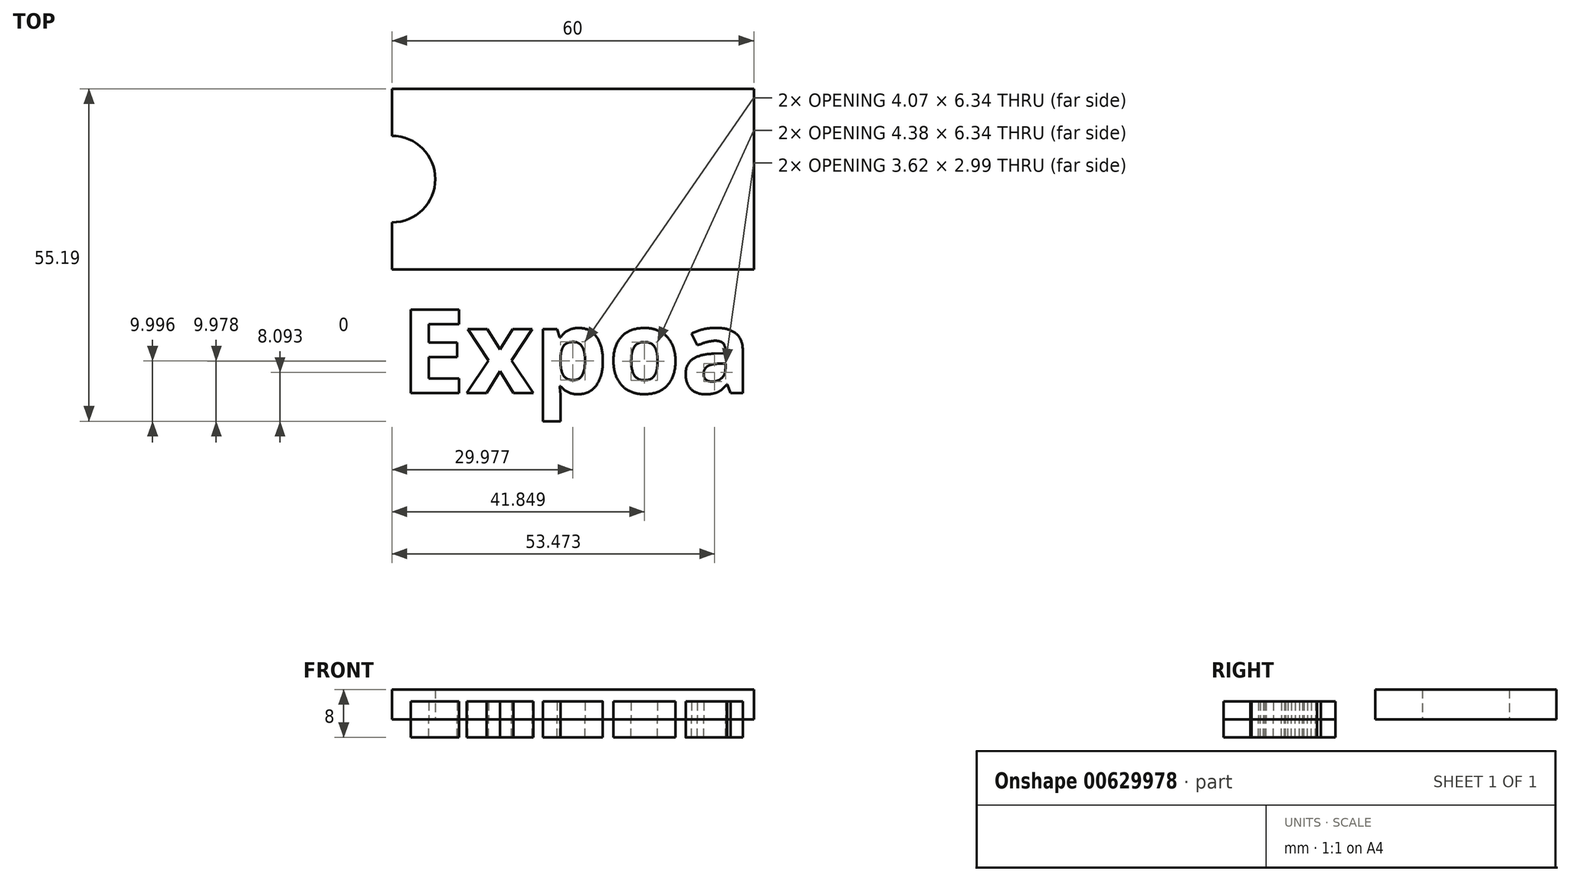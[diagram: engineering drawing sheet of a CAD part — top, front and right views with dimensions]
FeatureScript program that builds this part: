
annotation { "Feature Type Name" : "Feature", "Feature Type Description" : "" }
export const myFeature = defineFeature(function(context is Context, id is Id, definition is map)
    precondition{}
    {
        {
            var Q0;
            Q0=qCreatedBy(makeId("Top.planeOp"),FACE);
            var sketch = newSketch(context, id + "F0", { "sketchPlane" : qUnion([Q0])});
            skLineSegment(sketch, "E0.bottom", {"start": v(30, -15) * mm, "end": v(-30, -15) * mm});
            skLineSegment(sketch, "E0.top", {"start": v(30, 15) * mm, "end": v(-30, 15) * mm});
            skLineSegment(sketch, "E0.left", {"start": v(30, -15) * mm, "end": v(30, 15) * mm});
            skLineSegment(sketch, "E0.right", {"start": v(-30, -15) * mm, "end": v(-30, 15) * mm});
            skPoint(sketch, "E0.middle", {"position": v(0, 0) * mm});
            skCircle(sketch, "E1", {"center": v(-30, 0) * mm, "radius": 7.18 * mm});
            skSolve(sketch);
        }
        {
            var Q0;
            Q0=makeQuery(id+"F0.imprint","IMPRINT",FACE,{"disambiguationData":[TD([[makeQuery(id+"F0.imprint","IMPRINT",EDGE,{"derivedFrom":sQuery(id+"F0.wireOp",EDGE,"E0.bottom")}),-1.0]])]});
            extrude(context, id + "F1", {"entities" : qUnion([Q0]), "depth" : 5 * mm, "offsetDistance" : 25 * mm});
        }
        {
            var Q0;
            Q0=makeQuery(id+"F1.opExtrude","SWEPT_EDGE",EDGE,{"disambiguationData":[OSD([sQuery(id+"F0.wireOp",EDGE,"E0.bottom"),sQuery(id+"F0.wireOp",EDGE,"E0.right")])]});
            var Q1;
            Q1=makeQuery(id+"F1.opExtrude","SWEPT_EDGE",EDGE,{"disambiguationData":[OSD([sQuery(id+"F0.wireOp",EDGE,"E0.bottom"),sQuery(id+"F0.wireOp",EDGE,"E0.left")])]});
            var Q2;
            Q2=makeQuery(id+"F1.opExtrude","SWEPT_EDGE",EDGE,{"disambiguationData":[OSD([sQuery(id+"F0.wireOp",EDGE,"E0.top"),sQuery(id+"F0.wireOp",EDGE,"E0.left")])]});
            var Q3;
            Q3=makeQuery(id+"F1.opExtrude","SWEPT_EDGE",EDGE,{"disambiguationData":[OSD([sQuery(id+"F0.wireOp",EDGE,"E0.top"),sQuery(id+"F0.wireOp",EDGE,"E0.right")])]});
            fillet(context, id + "F2", {"entities" : qUnion([Q0, Q1, Q2, Q3]), "radius" : 5 * mm, "tangentPropagation" : true, "allowEdgeOverflow" : false});
        }
        {
            var Q0;
            {var subQ0=sQuery(id+"F0.wireOp",EDGE,"E1");var subQ1=sQuery(id+"F0.wireOp",EDGE,"E0.right");var subQ2=makeQuery(id+"F0.imprint","INTERSECT",VERTEX,{"disambiguationData":[OD(0.0)],"derivedFrom":[subQ1,subQ0]});Q0=makeQuery(id+"F0.imprint","IMPRINT",FACE,{"disambiguationData":[TD([[makeQuery(id+"F0.imprint","IMPRINT",EDGE,{"disambiguationData":[TD([[subQ2,-1.0]])],"derivedFrom":subQ1}),-1.0]])]});}
            var Q1;
            {var subQ0=sQuery(id+"F0.wireOp",EDGE,"E1");var subQ1=sQuery(id+"F0.wireOp",EDGE,"E0.right");var subQ2=makeQuery(id+"F0.imprint","INTERSECT",VERTEX,{"disambiguationData":[OD(0.0)],"derivedFrom":[subQ1,subQ0]});Q1=makeQuery(id+"F0.imprint","IMPRINT",FACE,{"disambiguationData":[TD([[makeQuery(id+"F0.imprint","IMPRINT",EDGE,{"disambiguationData":[TD([[subQ2,-1.0]])],"derivedFrom":subQ1}),1.0]])]});}
            extrude(context, id + "F3", {"entities" : qUnion([Q0, Q1]), "operationType" : NewBodyOperationType.ADD, "depth" : 5 * mm, "offsetDistance" : 25 * mm});
        }
        {
            var Q0;
            {var subQ0=sQuery(id+"F0.wireOp",EDGE,"E1");Q0=makeQuery(id+"F3.boolean.opBoolean","MERGE",FACE,{"derivedFrom":[makeQuery(id+"F1.opExtrude","CAP_FACE",FACE,{"disambiguationData":[OSD([sQuery(id+"F0.wireOp",EDGE,"E0.bottom"),sQuery(id+"F0.wireOp",EDGE,"E0.top"),sQuery(id+"F0.wireOp",EDGE,"E0.left"),sQuery(id+"F0.wireOp",EDGE,"E0.right"),subQ0])],"isStart":false}),makeQuery(id+"F3.opExtrude","CAP_FACE",FACE,{"disambiguationData":[OSD([subQ0])],"isStart":false})]});}
            var sketch = newSketch(context, id + "F4", { "sketchPlane" : qUnion([Q0])});
            skCircle(sketch, "E2", {"center": v(-31.84, 0) * mm, "radius": 1.79 * mm});
            skCircle(sketch, "E3", {"center": v(-31.84, 0) * mm, "radius": 3.5 * mm});
            skSolve(sketch);
        }
        {
            var Q0;
            Q0=makeQuery(id+"F4.imprint","IMPRINT",FACE,{"disambiguationData":[TD([[makeQuery(id+"F4.imprint","IMPRINT",EDGE,{"derivedFrom":sQuery(id+"F4.wireOp",EDGE,"E2")}),1.0]])]});
            extrude(context, id + "F5", {"entities" : qUnion([Q0]), "operationType" : NewBodyOperationType.REMOVE, "oppositeDirection" : true, "depth" : 25 * mm, "offsetDistance" : 25 * mm});
        }
        {
            var Q0;
            Q0=qCreatedBy(makeId("Top.planeOp"),FACE);
            var sketch = newSketch(context, id + "F6", { "sketchPlane" : qUnion([Q0])});
            skText(sketch, "E4", { "text": "Expoa", "fontName": "OpenSans-Bold.ttf"});
            const initialGuessF6  = {"E4": [-0.0286, -0.03552, 1, 0, 0.014]};
            skSetInitialGuess(sketch, initialGuessF6);
            skSolve(sketch);
        }
        {
            var Q0;
            Q0=makeQuery(id+"F6.imprint","IMPRINT",FACE,{"disambiguationData":[TD([[makeQuery(id+"F6.imprint","IMPRINT",EDGE,{"derivedFrom":sQuery(id+"F6.wireOp",EDGE,"E4.sketch_text.stroke-0")}),-1.0]])]});
            var Q1;
            Q1=makeQuery(id+"F6.imprint","IMPRINT",FACE,{"disambiguationData":[TD([[makeQuery(id+"F6.imprint","IMPRINT",EDGE,{"derivedFrom":sQuery(id+"F6.wireOp",EDGE,"E4.sketch_text.stroke-12")}),-1.0]])]});
            var Q2;
            Q2=makeQuery(id+"F6.imprint","IMPRINT",FACE,{"disambiguationData":[TD([[makeQuery(id+"F6.imprint","IMPRINT",EDGE,{"derivedFrom":sQuery(id+"F6.wireOp",EDGE,"E4.sketch_text.stroke-24")}),-1.0]])]});
            var Q3;
            Q3=makeQuery(id+"F6.imprint","IMPRINT",FACE,{"disambiguationData":[TD([[makeQuery(id+"F6.imprint","IMPRINT",EDGE,{"derivedFrom":sQuery(id+"F6.wireOp",EDGE,"E4.sketch_text.stroke-47")}),-1.0]])]});
            var Q4;
            Q4=makeQuery(id+"F6.imprint","IMPRINT",FACE,{"disambiguationData":[TD([[makeQuery(id+"F6.imprint","IMPRINT",EDGE,{"derivedFrom":sQuery(id+"F6.wireOp",EDGE,"E4.sketch_text.stroke-65")}),-1.0]])]});
            extrude(context, id + "F7", {"entities" : qUnion([Q0, Q1, Q2, Q3, Q4]), "operationType" : NewBodyOperationType.ADD, "oppositeDirection" : true, "depth" : 3 * mm, "offsetDistance" : 25 * mm});
        }
        {
            var Q0;
            Q0=makeQuery(id+"F4.imprint","IMPRINT",FACE,{"disambiguationData":[TD([[makeQuery(id+"F4.imprint","IMPRINT",EDGE,{"derivedFrom":sQuery(id+"F4.wireOp",EDGE,"E2")}),-1.0]])]});
            var Q1;
            Q1=makeQuery(id+"F4.imprint","IMPRINT",FACE,{"disambiguationData":[TD([[makeQuery(id+"F4.imprint","IMPRINT",EDGE,{"derivedFrom":sQuery(id+"F4.wireOp",EDGE,"E2")}),1.0]])]});
            extrude(context, id + "F8", {"entities" : qUnion([Q0, Q1]), "operationType" : NewBodyOperationType.REMOVE, "oppositeDirection" : true, "depth" : 25 * mm, "offsetDistance" : 25 * mm});
        }
        {
            var Q0;
            Q0 = qSketchRegion(id + "F6", true);
            extrude(context, id + "F9", {"entities" : qUnion([Q0]), "depth" : 3 * mm, "offsetDistance" : 25 * mm});
        }
    });
